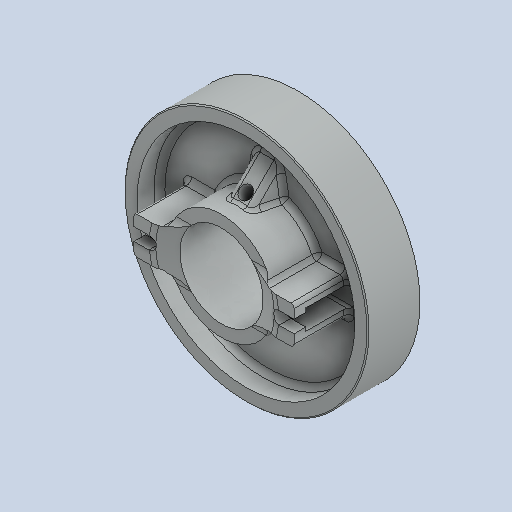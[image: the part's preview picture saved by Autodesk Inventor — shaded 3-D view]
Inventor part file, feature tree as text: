
AUTODESK INVENTOR PART (.ipt)
format: ipt  version: 2024.1 (Build 281209000, 209)  size: 379,904 bytes
history: native  units: in
note: dims shown in document units (in); Inventor stores cm internally (conversion verified against a paired STEP export)
features: fillet x1
ambient origin geometry x8: Origin, YZ Plane, XZ Plane, XY Plane, X Axis, Y Axis, Z Axis, Center Point
bodies: Solid1 (feature_tree)
feature tree (1):
  fillet  "Fillet23"  [1 undecoded]
note: 1 required parameter value undecoded (feature->parameter linkage not recoverable at this tier; creation-order binding heuristic only, values carry confidence <= 0.55)
